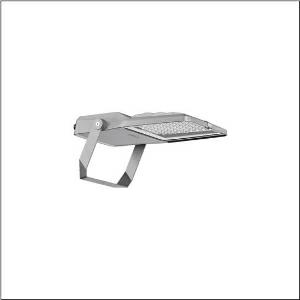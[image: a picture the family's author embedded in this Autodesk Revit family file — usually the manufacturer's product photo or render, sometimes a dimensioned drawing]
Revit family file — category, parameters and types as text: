
# Revit family: floodlight_fl_21_iq_mini___pl43_5xa7772c3a1a_2542
name_source: partatom
category: Lighting Fixtures
units: mm (PartAtom-declared; Revit-internal decimal feet)

## family parameters
Cut with Voids When Loaded = No
Host = Face
Light Source = No
Part Type = Normal
Room Calculation Point = No
Round Connector Dimension = Use Diameter
Shared = No

## types (1)
- --- (1 x LED, 10780 lm, 87.2 W, 3000K)
    Apparent Load = 87 VA
    CIE Flux Codes = 27 78 99 100 100
    Color Rendering = 80
    Color Temperature = 3000K
    Default Elevation = 1800 mm
    Description = Floodlight FL 21 iQ mini, floodlight, primary light control with lens, of PMMA, primary optical cover: protective disc, of toughened safety glass, transparent, light distribution: PL43, light emission: direct distribution, installation type: surface-mounted, LED, High Power LED, rated luminous flux: 10.780lm, luminous efficacy: 124lm/W, light colour: 830, colour temperature: 3000K, control gear: iQ Street-Remote/DALI, control: Street-Remote, Auto-Match, Temp-Guard, Night-Set, Smart-Wire, Desk-Remote (wireless, voltage-free reading and setting of iQ features in the workshop via application-optimized NFC function/RFID function), optimised constant luminous flux control (CLO 2.0), with terminal, 6-pole, mains connection: 220..240V, AC, 50/60Hz, start of lifetime: 87W, end of service life: 92W, reduction: 40W, luminaire housing, of diecast aluminium, powder-coated, Siteco® metallic grey (DB 702S), corrosivity category C5 mid according to DIN EN ISO 12944, suitable for swimming pools, chlorine-resistant, sealing non-destructively replaceable, mounting bracket, of steel, galvanised, powder-coated, Siteco® metallic grey (DB 702S), protection rating (complete): IP66, insulation class (complete): insulation class II (safety insulation), certification: CE, ENEC, VDE, protection symbol: D, impact resistance: IK08, permissible operating ambient temperature: -40..+40°C, permissible operating ambient temperature for outdoor applications: -40..+50°C, standard: DIN EN 12944, LABS conformity tested according to VDMA 24364:2018-05, packaging unit: 1 piece

Light Distribution: PL43
    Height = 70 mm
    Lamp = 1 x LED
    Lamp Light Flux = 10780 lm
    Lamp Power = 87.2 W
    Lamp count = 1
    Length = 485 mm
    Luminous efficacy = 124 lm/W
    Manufacturer = Siteco
    ModVariant = No
    Model = 5XA7772C3A1A
    Number of Poles = 1
    OnlyDefault = Yes
    Power Factor = 1
    Product Name = Floodlight FL 21 iQ mini | PL43
    Product group = floodlight | pylon annexe
    ProductGroupID = 6200
    Protection Class = Protection class II
    Protection Degree = IP 66
    RLX_Detail_Level = 1
    RLX_Emergency_Light_Flux = 0 lm
    RLX_Emergency_Type = 0
    RLX_Emergency_Type_DB = No
    RlxData = <blob elided: 96285 chars, md5=6afa6b86>
    Socket = socket
    Standby Power = 0 W
    System Light Flux = 10780 lm
    System Power = 87 W
    Type Comments = factory setting: luminous flux: 100 % | dim-lin: 254 | 456 mA
    Type Image = l_1006845.jpg
    URL = http://relux.com
    VarID = @adj_162270
    Voltage = 0 V
    Weight = 0.00 kg
    Width = 337 mm

## geometry (parser evidence)
native form markers: Blend x4, Sweep x12
no freeform markers — native parametric forms only
